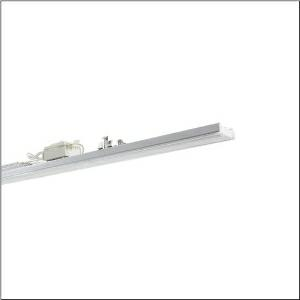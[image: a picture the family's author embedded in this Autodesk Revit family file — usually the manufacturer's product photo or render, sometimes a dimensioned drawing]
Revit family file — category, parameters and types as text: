
# Revit family: licross_21_recessed_mo_51te12vn48xg
name_source: partatom
category: Lighting Fixtures
units: mm (PartAtom-declared; Revit-internal decimal feet)

## family parameters
Cut with Voids When Loaded = No
Host = Face
Light Source = No
Part Type = Normal
Room Calculation Point = No
Round Connector Dimension = Use Diameter
Shared = No

## types (1)
- --- (1 x LED, 8000 lm, 43.4 W, 4000K)
    Apparent Load = 43 VA
    CIE Flux Codes = 67 92 99 100 100
    Color Rendering = 80
    Color Temperature = 4000K
    Default Elevation = 1800 mm
    Description = Licross 21 Recessed MO, luminaire insert, of sheet steel, galvanised, coil coated, white, length: 1.500mm, width: 66mm, height: 67mm, LED rated luminous flux: 8.000lm, light colour: 840, SDCM (Standard Deviation of Colour Matching)MacAdam ≤ 2 SDCM (initial), control gear: DALI 2, CLO, with plug, 5-pole, with phase selection, mains connection: 220..240V, AC, 50/60Hz, start of lifetime: 43W, end of service life: 48W, internal wiring halogen-free, primary optical cover: cover, of PMMA, light emission: direct distribution, primary light characteristic: symmetric, protection rating (complete): IP54, insulation class (complete): insulation class I (protective earthing), certification: CE, ENEC, VDE, UKCA, protection symbol: D if used in an environment with non-conductive dust loads with corresponding accessories, impact resistance: IK06, permissible ambient temperature for indoor applications: -25..+35°C, corresponds to IFS (International Featured Standards) requirements for safety and quality in the food industry, reducing of maximum allowable ambient temperature of 5°C with ceiling mounting, LABS conformity tested according to VDMA 24364:2018-05, The light source and the operating device comply with the requirements of the Ecodesign Regulation (EU) 2019/2020 and are replaceable in accordance with this regulation, packaging unit: 1 piece
    Height = 58 mm
    Lamp = 1 x LED
    Lamp Light Flux = 8000 lm
    Lamp Power = 43.4 W
    Lamp count = 1
    Length = 1500 mm
    Luminous efficacy = 184 lm/W
    Manufacturer = Siteco
    ModVariant = No
    Model = 51TE12VN48XG
    Mounting Place = Ceiling
    Mounting Type = Pendant
    Number of Poles = 1
    OnlyDefault = Yes
    Power Factor = 1
    Product Name = Licross 21 Recessed MO
    Product group = luminaire insert | ceiling pendant
    ProductGroupID = 901
    Protection Class = Protection class I
    Protection Degree = IP 54
    RLX_Detail_Level = 1
    RLX_Emergency_Light_Flux = 0 lm
    RLX_Emergency_Type = 0
    RLX_Emergency_Type_DB = No
    RlxData = <blob elided: 24685 chars, md5=1a2e50d7>
    Socket = socket
    Standby Power = 0 W
    System Light Flux = 8000 lm
    System Power = 43 W
    Type Comments = factory setting: luminous flux: 100 % | dim-lin: 254 | 289 mA
    Type Image = l_1296930.jpg
    URL = http://relux.com
    VarID = @adj_092777
    Voltage = 0 V
    Weight = 0.00 kg
    Width = 66 mm

## geometry (parser evidence)
native form markers: Blend x4, Sweep x10
no freeform markers — native parametric forms only
